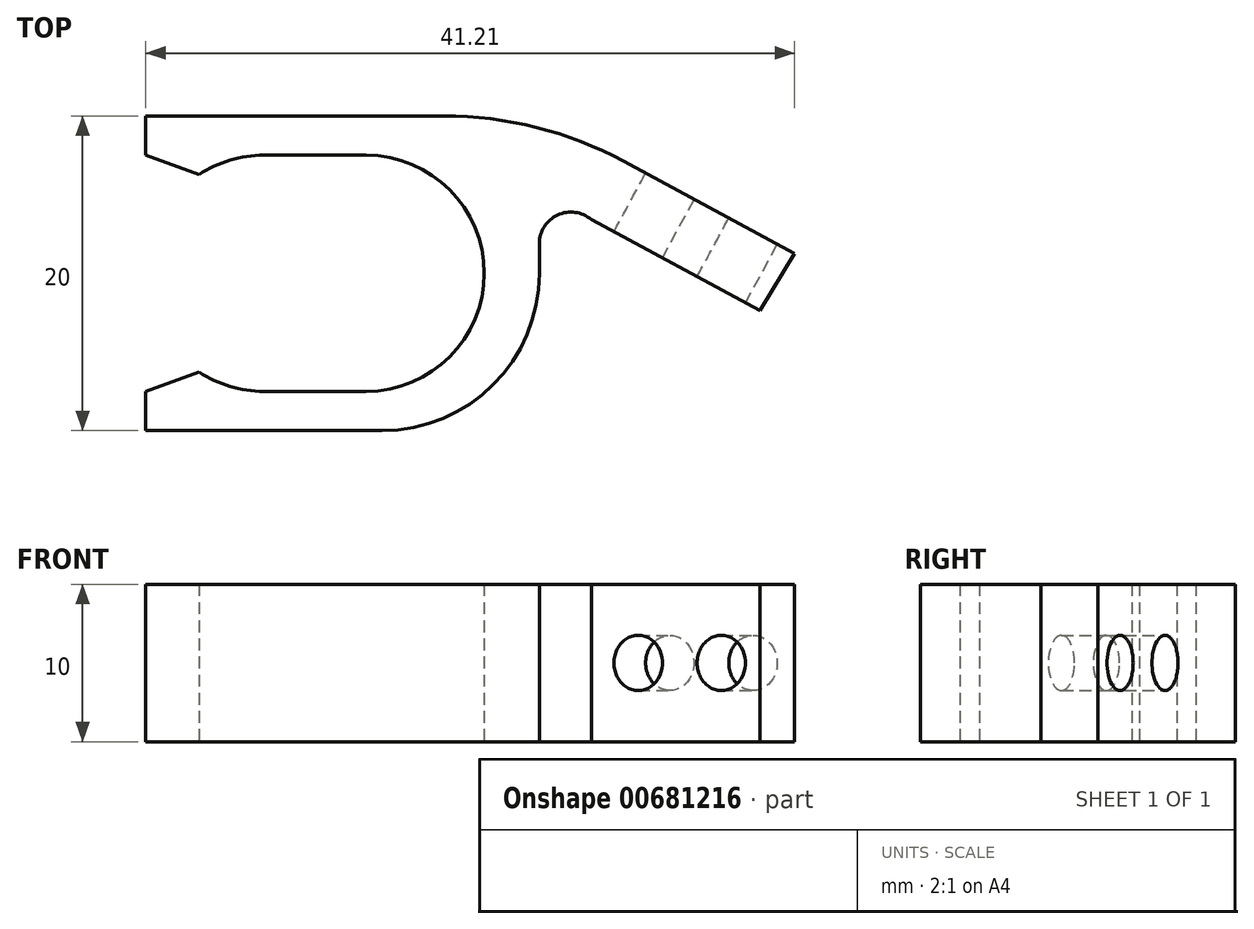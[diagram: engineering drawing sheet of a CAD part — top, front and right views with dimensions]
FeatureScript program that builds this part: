
annotation { "Feature Type Name" : "Feature", "Feature Type Description" : "" }
export const myFeature = defineFeature(function(context is Context, id is Id, definition is map)
    precondition{}
    {
        {
            var Q0;
            Q0=qCreatedBy(makeId("Top.planeOp"),FACE);
            var sketch = newSketch(context, id + "F0", { "sketchPlane" : qUnion([Q0])});
            skLineSegment(sketch, "E0.bottom", {"start": v(0, 20) * mm, "end": v(-25, 20) * mm});
            skLineSegment(sketch, "E0.top", {"start": v(-10, 0) * mm, "end": v(-25, 0) * mm});
            skLineSegment(sketch, "E0.left", {"start": v(0, 11.89) * mm, "end": v(0, 10) * mm});
            skLineSegment(sketch, "E0.right", {"start": v(-25, 20) * mm, "end": v(-25, 0) * mm});
            skLineSegment(sketch, "E1", {"start": v(-25, 17.5) * mm, "end": v(-3.5, 17.5) * mm});
            skLineSegment(sketch, "E2", {"start": v(-3.5, 17.5) * mm, "end": v(-3.5, 2.5) * mm});
            skLineSegment(sketch, "E3", {"start": v(-3.5, 2.5) * mm, "end": v(-25, 2.5) * mm});
            skLineSegment(sketch, "E4", {"start": v(-25, 10) * mm, "end": v(-4.71, 10) * mm, "construction": true});
            skCircle(sketch, "E5", {"center": v(-11, 10) * mm, "radius": 7.5 * mm});
            skCircle(sketch, "E6", {"center": v(-17.5, 10) * mm, "radius": 7.5 * mm});
            skLineSegment(sketch, "E7", {"start": v(-21.61, 16.27) * mm, "end": v(-25, 17.5) * mm});
            skLineSegment(sketch, "E8.MirrorCS", {"start": v(-21.61, 3.73) * mm, "end": v(-25, 2.5) * mm});
            skLineSegment(sketch, "E9", {"start": v(0, 20) * mm, "end": v(16.2, 11.25) * mm});
            skPoint(sketch, "E10.newPointA", {"position": v(0, 13.75) * mm});
            skPoint(sketch, "E10.newPointB", {"position": v(0, 20) * mm});
            skArc(sketch, "E10.filletArc", {"start": v(3.3, 13.41) * mm, "mid": v(1.16, 13.7) * mm, "end": v(0, 11.89) * mm});
            skPoint(sketch, "E11.visualSharp", {"position": v(0, 0) * mm});
            skArc(sketch, "E11.filletArc", {"start": v(-10, 0) * mm, "mid": v(-2.93, 2.93) * mm, "end": v(0, 10) * mm});
            skLineSegment(sketch, "E12", {"start": v(3.3, 13.41) * mm, "end": v(14, 7.63) * mm});
            skLineSegment(sketch, "E13", {"start": v(14, 7.63) * mm, "end": v(16.2, 11.25) * mm});
            skSolve(sketch);
        }
        {
            var Q0;
            {var subQ0=sQuery(id+"F0.wireOp",EDGE,"524256dc-d7f1-4f18-900e-8b40193f3f63");Q0=makeQuery(id+"F0.imprint","IMPRINT",FACE,{"disambiguationData":[TD([[makeQuery(id+"F0.imprint","IMPRINT",EDGE,{"derivedFrom":subQ0}),1.0]])]});}
            var Q1;
            {var subQ1=sQuery(id+"F0.wireOp",EDGE,"E0.bottom");Q1=makeQuery(id+"F0.imprint","IMPRINT",FACE,{"disambiguationData":[TD([[makeQuery(id+"F0.imprint","IMPRINT",EDGE,{"derivedFrom":subQ1}),1.0]])]});}
            var Q2;
            {var subQ0=sQuery(id+"F0.wireOp",EDGE,"694dbbf3-e233-4638-8b07-2db61897eeeb.MirrorCS");Q2=makeQuery(id+"F0.imprint","IMPRINT",FACE,{"disambiguationData":[TD([[makeQuery(id+"F0.imprint","IMPRINT",EDGE,{"derivedFrom":subQ0}),-1.0]])]});}
            var Q3;
            Q3=makeQuery(id+"F0.imprint","IMPRINT",FACE,{"disambiguationData":[TD([[makeQuery(id+"F0.imprint","IMPRINT",EDGE,{"derivedFrom":sQuery(id+"F0.wireOp",EDGE,"E0.left")}),1.0]])]});
            var Q4;
            {var subQ0=sQuery(id+"F0.wireOp",EDGE,"E7");Q4=makeQuery(id+"F0.imprint","IMPRINT",FACE,{"disambiguationData":[TD([[makeQuery(id+"F0.imprint","IMPRINT",EDGE,{"derivedFrom":subQ0}),-1.0]])]});}
            var Q5;
            {var subQ0=sQuery(id+"F0.wireOp",EDGE,"E8.MirrorCS");Q5=makeQuery(id+"F0.imprint","IMPRINT",FACE,{"disambiguationData":[TD([[makeQuery(id+"F0.imprint","IMPRINT",EDGE,{"derivedFrom":subQ0}),1.0]])]});}
            var Q6;
            {var subQ0=sQuery(id+"F0.wireOp",EDGE,"E2");var subQ1=sQuery(id+"F0.wireOp",EDGE,"E1");var subQ2=makeQuery(id+"F0.imprint","INTERSECT",VERTEX,{"derivedFrom":[subQ1,subQ0]});Q6=makeQuery(id+"F0.imprint","IMPRINT",FACE,{"disambiguationData":[TD([[makeQuery(id+"F0.imprint","IMPRINT",EDGE,{"disambiguationData":[TD([[subQ2,1.0]])],"derivedFrom":subQ1}),-1.0]])]});}
            var Q7;
            {var subQ0=sQuery(id+"F0.wireOp",EDGE,"E3");var subQ1=sQuery(id+"F0.wireOp",EDGE,"E2");var subQ2=makeQuery(id+"F0.imprint","INTERSECT",VERTEX,{"derivedFrom":[subQ1,subQ0]});Q7=makeQuery(id+"F0.imprint","IMPRINT",FACE,{"disambiguationData":[TD([[makeQuery(id+"F0.imprint","IMPRINT",EDGE,{"disambiguationData":[TD([[subQ2,1.0]])],"derivedFrom":subQ1}),-1.0]])]});}
            extrude(context, id + "F1", {"entities" : qUnion([Q0, Q1, Q2, Q3, Q4, Q5, Q6, Q7]), "endBound" : BoundingType.SYMMETRIC, "depth" : 10 * mm, "offsetDistance" : 25 * mm});
        }
        {
            var Q0;
            Q0=makeQuery(id+"F1.opExtrude","SWEPT_FACE",FACE,{"disambiguationData":[OSD([sQuery(id+"F0.wireOp",EDGE,"E9")])]});
            var sketch = newSketch(context, id + "F2", { "sketchPlane" : qUnion([Q0])});
            skCircle(sketch, "E14", {"center": v(-5.92, 0) * mm, "radius": 1.75 * mm});
            skCircle(sketch, "E15", {"center": v(0.08, 0) * mm, "radius": 1.75 * mm});
            skSolve(sketch);
        }
        {
            var Q0;
            Q0=makeQuery(id+"F2.imprint","IMPRINT",FACE,{"disambiguationData":[TD([[makeQuery(id+"F2.imprint","IMPRINT",EDGE,{"derivedFrom":sQuery(id+"F2.wireOp",EDGE,"E14")}),1.0]])]});
            var Q1;
            Q1=makeQuery(id+"F2.imprint","IMPRINT",FACE,{"disambiguationData":[TD([[makeQuery(id+"F2.imprint","IMPRINT",EDGE,{"derivedFrom":sQuery(id+"F2.wireOp",EDGE,"E15")}),1.0]])]});
            extrude(context, id + "F3", {"entities" : qUnion([Q0, Q1]), "operationType" : NewBodyOperationType.REMOVE, "oppositeDirection" : true, "depth" : 9.9 * mm, "offsetDistance" : 25 * mm});
        }
        {
            var Q0;
            Q0=makeQuery(id+"F1.opExtrude","SWEPT_EDGE",EDGE,{"disambiguationData":[OSD([sQuery(id+"F0.wireOp",EDGE,"E0.bottom"),sQuery(id+"F0.wireOp",EDGE,"E9")])]});
            fillet(context, id + "F4", {"entities" : qUnion([Q0]), "radius" : 24 * mm, "tangentPropagation" : true, "allowEdgeOverflow" : false});
        }
    });
